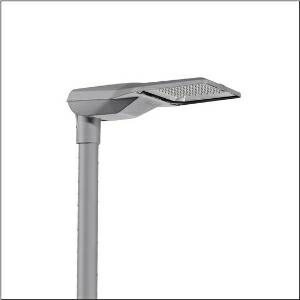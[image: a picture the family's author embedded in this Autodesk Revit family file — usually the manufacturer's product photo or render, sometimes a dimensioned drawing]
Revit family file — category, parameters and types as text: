
# Revit family: streetlight_sl_21_iq_midi___p0_8ab_5xe3r31g08mb_fd1f
name_source: partatom
category: Lighting Fixtures
units: mm (PartAtom-declared; Revit-internal decimal feet)

## family parameters
Cut with Voids When Loaded = No
Host = Face
Light Source = No
Part Type = Normal
Room Calculation Point = No
Round Connector Dimension = Use Diameter
Shared = No

## types (1)
- --- (1 x LED, 16930 lm, 146.7 W, 3000K)
    Apparent Load = 147 VA
    CIE Flux Codes = 36 71 98 100 100
    Color Rendering = 70
    Color Temperature = 3000K
    Default Elevation = 1800 mm
    Description = Streetlight SL 21 iQ midi, mast luminaire, primary light control with lens, of PMMA, primary optical cover: cover, of toughened safety glass, transparent, light distribution: P0.8aB, light emission: direct distribution, primary light characteristic: asymmetric, installation type: post-top, side-entry, LED, High Power LED, rated luminous flux: 16.930lm, luminous efficacy: 115lm/W, light colour: 730, colour temperature: 3000K, control gear: iQ Street-Remote, control: pre-setting: linear dimming characteristic, Street-Remote, Auto-Match, Temp-Guard, Lumen-Switch, Night-Set, Smart-Wire, Light-Fading, Desk-Remote (wireless, voltage-free reading and setting of iQ features in the workshop via application-optimized NFC function/RFID function), optimised constant luminous flux control (CLO 2.0), mains connection: 230..240V, AC, 50/60Hz, start of lifetime: 147W, end of service life: 161W, reduction: 62W, luminaire housing, of diecast aluminium, powder-coated, Siteco® metallic grey (DB 702S), corrosivity category C5 mid according to DIN EN ISO 12944, please order mast flange separately, inclination adjustable: 0°, 5°, 10°, 15°, sealing non-destructively replaceable, multi-level sealing system, length: 644mm, width: 335mm, height: 110mm, mast flange for spigot size: 42mm (side-entry): 5XC10008XM4, 60/48mm (side-entry/post-top): 5XC10108XM2, 76/60mm (side-entry/post-top): 5XC10108XM1, mounting height: 4..8m, protection rating (complete): IP66, insulation class (complete): insulation class II (safety insulation), certification: CE, ENEC, ENEC+, VDE, impact resistance: IK10, permissible operating ambient temperature for outdoor applications: -40..+50°C, standard-compliant lighting for roads and squares, packaging unit: 1 piece

Light Distribution: P0.8aB
    Height = 111 mm
    Lamp = 1 x LED
    Lamp Light Flux = 16930 lm
    Lamp Power = 146.7 W
    Lamp count = 1
    Length = 644 mm
    Luminous efficacy = 115 lm/W
    Manufacturer = Siteco
    ModVariant = No
    Model = 5XE3R31G08MB
    Number of Poles = 1
    OnlyDefault = Yes
    Power Factor = 1
    Product Name = Streetlight SL 21 iQ midi | P0.8aB
    Product group = mast luminaire | pylon top
    ProductGroupID = 6100
    Protection Class = Protection class II
    Protection Degree = IP 66
    RLX_Detail_Level = 1
    RLX_Emergency_Light_Flux = 0 lm
    RLX_Emergency_Type = 0
    RLX_Emergency_Type_DB = No
    RlxData = <blob elided: 90649 chars, md5=3f571c02>
    Socket = socket
    Standby Power = 0 W
    System Light Flux = 16931 lm
    System Power = 147 W
    Type Comments = factory setting: luminous flux: 100 % | dim-lin: 254 | 753 mA
    Type Image = l_1004298.jpg
    URL = http://relux.com
    VarID = @adj_095893
    Voltage = 0 V
    Weight = 0.00 kg
    Width = 336 mm

## geometry (parser evidence)
native form markers: Blend x4, Sweep x10
no freeform markers — native parametric forms only
